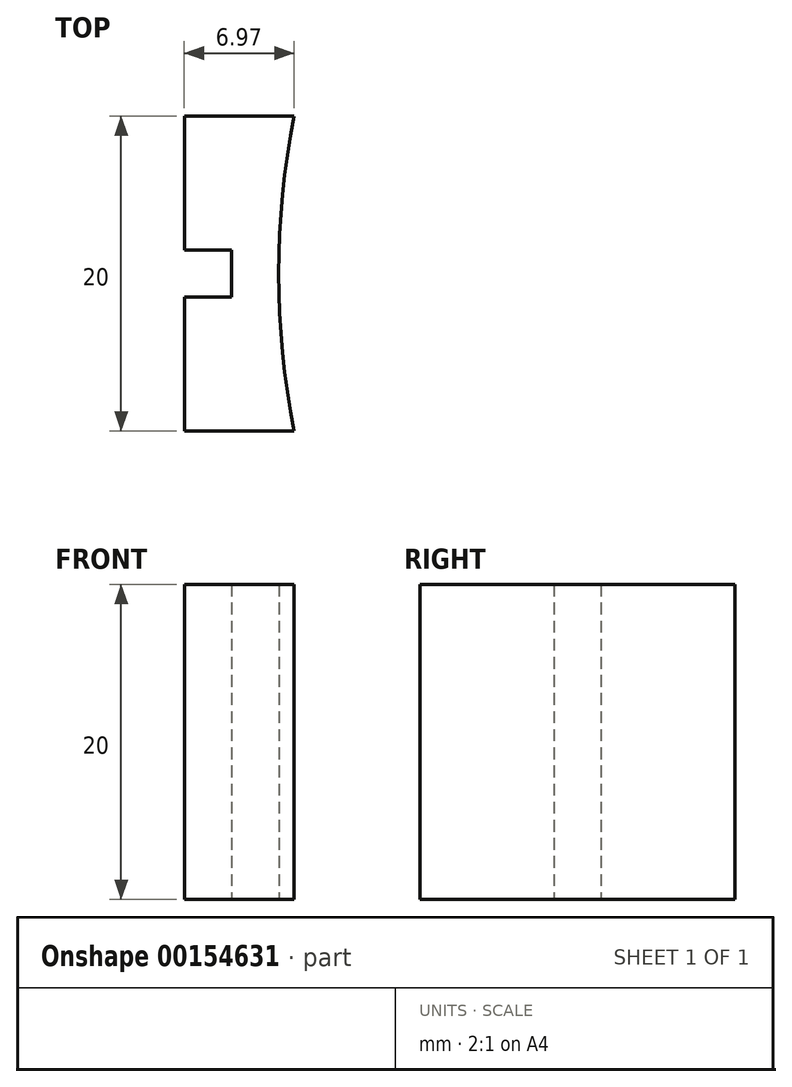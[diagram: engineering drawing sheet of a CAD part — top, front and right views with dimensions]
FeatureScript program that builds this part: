
annotation { "Feature Type Name" : "Feature", "Feature Type Description" : "" }
export const myFeature = defineFeature(function(context is Context, id is Id, definition is map)
    precondition{}
    {
        {
            var Q0;
            Q0=qCreatedBy(makeId("Top.planeOp"),FACE);
            var sketch = newSketch(context, id + "F0", { "sketchPlane" : qUnion([Q0])});
            skArc(sketch, "E0", {"start": v(-51.42, 10) * mm, "mid": v(-52.39, 0) * mm, "end": v(-51.42, -10) * mm});
            skLineSegment(sketch, "E1", {"start": v(-55.39, 0) * mm, "end": v(-55.39, 10) * mm});
            skLineSegment(sketch, "E2", {"start": v(-55.39, 10) * mm, "end": v(-51.42, 10) * mm});
            skLineSegment(sketch, "E3.MirrorCS", {"start": v(-55.39, -10) * mm, "end": v(-51.42, -10) * mm});
            skLineSegment(sketch, "E4.MirrorCS", {"start": v(-55.39, 0) * mm, "end": v(-55.39, -10) * mm});
            skSolve(sketch);
        }
        {
            var Q0;
            Q0=makeQuery(id+"F0.imprint","IMPRINT",FACE,{"disambiguationData":[TD([[makeQuery(id+"F0.imprint","IMPRINT",EDGE,{"derivedFrom":sQuery(id+"F0.wireOp",EDGE,"E0")}),-1.0]])]});
            extrude(context, id + "F1", {"entities" : qUnion([Q0]), "depth" : 20 * mm});
        }
        {
            var Q0;
            Q0=makeQuery(id+"F1.opExtrude","SWEPT_FACE",FACE,{"disambiguationData":[OSD([sQuery(id+"F0.wireOp",EDGE,"E1"),sQuery(id+"F0.wireOp",EDGE,"E4.MirrorCS")])]});
            var sketch = newSketch(context, id + "F2", { "sketchPlane" : qUnion([Q0])});
            skLineSegment(sketch, "E5", {"start": v(0, 20) * mm, "end": v(1.5, 20) * mm});
            skLineSegment(sketch, "E6", {"start": v(1.5, 20) * mm, "end": v(1.5, 0) * mm});
            skLineSegment(sketch, "E7", {"start": v(1.5, 0) * mm, "end": v(0, 0) * mm});
            skLineSegment(sketch, "E8.MirrorCS", {"start": v(0, 20) * mm, "end": v(-1.5, 20) * mm});
            skLineSegment(sketch, "E9.MirrorCS", {"start": v(-1.5, 20) * mm, "end": v(-1.5, 0) * mm});
            skLineSegment(sketch, "E10.MirrorCS", {"start": v(-1.5, 0) * mm, "end": v(0, 0) * mm});
            skSolve(sketch);
        }
        {
            var Q0;
            {var subQ0=sQuery(id+"F2.wireOp",EDGE,"E6");Q0=makeQuery(id+"F2.imprint","IMPRINT",FACE,{"disambiguationData":[TD([[makeQuery(id+"F2.imprint","IMPRINT",EDGE,{"derivedFrom":subQ0}),1.0]])]});}
            var Q1;
            {var subQ0=sQuery(id+"F2.wireOp",EDGE,"E9.MirrorCS");Q1=makeQuery(id+"F2.imprint","IMPRINT",FACE,{"disambiguationData":[TD([[makeQuery(id+"F2.imprint","IMPRINT",EDGE,{"derivedFrom":subQ0}),-1.0]])]});}
            extrude(context, id + "F3", {"entities" : qUnion([Q0, Q1]), "operationType" : NewBodyOperationType.ADD, "depth" : 3 * mm});
        }
    });
